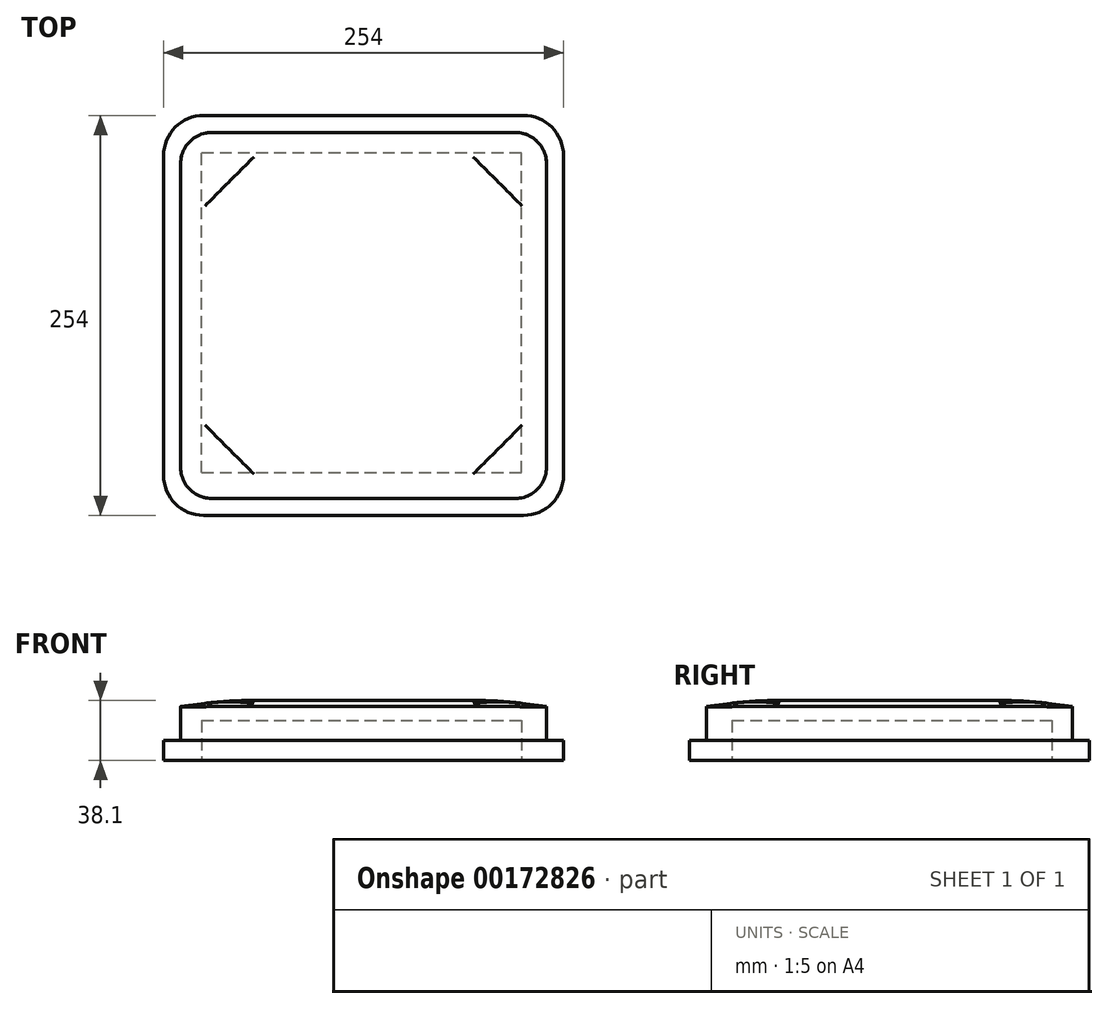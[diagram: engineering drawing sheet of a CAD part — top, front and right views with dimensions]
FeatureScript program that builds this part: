
annotation { "Feature Type Name" : "Feature", "Feature Type Description" : "" }
export const myFeature = defineFeature(function(context is Context, id is Id, definition is map)
    precondition{}
    {
        {
            var Q0;
            Q0=qCreatedBy(makeId("Top.planeOp"),FACE);
            var sketch = newSketch(context, id + "F0", { "sketchPlane" : qUnion([Q0])});
            skLineSegment(sketch, "E0.bottom", {"start": v(-176.99, 231.22) * mm, "end": v(26.21, 231.22) * mm});
            skLineSegment(sketch, "E0.top", {"start": v(-176.99, -22.78) * mm, "end": v(26.21, -22.78) * mm});
            skLineSegment(sketch, "E0.left", {"start": v(-202.39, 205.82) * mm, "end": v(-202.39, 2.62) * mm});
            skLineSegment(sketch, "E0.right", {"start": v(51.61, 205.82) * mm, "end": v(51.61, 2.62) * mm});
            skPoint(sketch, "E1.visualSharp", {"position": v(-202.39, 231.22) * mm});
            skArc(sketch, "E1.filletArc", {"start": v(-176.99, 231.22) * mm, "mid": v(-194.95, 223.78) * mm, "end": v(-202.39, 205.82) * mm});
            skPoint(sketch, "E2.visualSharp", {"position": v(51.61, 231.22) * mm});
            skArc(sketch, "E2.filletArc", {"start": v(51.61, 205.82) * mm, "mid": v(44.17, 223.78) * mm, "end": v(26.21, 231.22) * mm});
            skPoint(sketch, "E3.visualSharp", {"position": v(51.61, -22.78) * mm});
            skArc(sketch, "E3.filletArc", {"start": v(26.21, -22.78) * mm, "mid": v(44.17, -15.34) * mm, "end": v(51.61, 2.62) * mm});
            skPoint(sketch, "E4.visualSharp", {"position": v(-202.39, -22.78) * mm});
            skArc(sketch, "E4.filletArc", {"start": v(-202.39, 2.62) * mm, "mid": v(-194.95, -15.34) * mm, "end": v(-176.99, -22.78) * mm});
            skSolve(sketch);
        }
        {
            var Q0;
            Q0=qCreatedBy(makeId("Top.planeOp"),FACE);
            var sketch = newSketch(context, id + "F1", { "sketchPlane" : qUnion([Q0])});
            skLineSegment(sketch, "E5.bottom", {"start": v(-171.78, 220.42) * mm, "end": v(21, 220.42) * mm});
            skLineSegment(sketch, "E5.top", {"start": v(-171.78, -11.99) * mm, "end": v(21, -11.99) * mm});
            skLineSegment(sketch, "E5.left", {"start": v(-191.6, 200.61) * mm, "end": v(-191.6, 7.83) * mm});
            skLineSegment(sketch, "E5.right", {"start": v(40.82, 200.61) * mm, "end": v(40.82, 7.83) * mm});
            skPoint(sketch, "E6.visualSharp", {"position": v(-191.6, 220.42) * mm});
            skArc(sketch, "E6.filletArc", {"start": v(-171.78, 220.42) * mm, "mid": v(-185.8, 214.62) * mm, "end": v(-191.6, 200.61) * mm});
            skPoint(sketch, "E7.visualSharp", {"position": v(40.82, 220.42) * mm});
            skArc(sketch, "E7.filletArc", {"start": v(40.82, 200.61) * mm, "mid": v(35.01, 214.62) * mm, "end": v(21, 220.42) * mm});
            skPoint(sketch, "E8.visualSharp", {"position": v(40.82, -11.99) * mm});
            skArc(sketch, "E8.filletArc", {"start": v(21, -11.99) * mm, "mid": v(35.01, -6.18) * mm, "end": v(40.82, 7.83) * mm});
            skPoint(sketch, "E9.visualSharp", {"position": v(-191.6, -11.99) * mm});
            skArc(sketch, "E9.filletArc", {"start": v(-191.6, 7.83) * mm, "mid": v(-185.8, -6.18) * mm, "end": v(-171.78, -11.99) * mm});
            skSolve(sketch);
        }
        {
            var Q0;
            Q0 = qSketchRegion(id + "F0", true);
            extrude(context, id + "F2", {"entities" : qUnion([Q0]), "depth" : 25.4 * mm});
        }
        {
            var Q0;
            Q0 = qSketchRegion(id + "F1", true);
            extrude(context, id + "F3", {"entities" : qUnion([Q0]), "operationType" : NewBodyOperationType.ADD, "depth" : 47 * mm});
        }
        {
            var Q0;
            Q0=makeQuery(id+"F3.opExtrude","CAP_FACE",FACE,{"disambiguationData":[OSD([sQuery(id+"F1.wireOp",EDGE,"E5.bottom"),sQuery(id+"F1.wireOp",EDGE,"E5.top"),sQuery(id+"F1.wireOp",EDGE,"E5.left"),sQuery(id+"F1.wireOp",EDGE,"E5.right"),sQuery(id+"F1.wireOp",EDGE,"E6.filletArc"),sQuery(id+"F1.wireOp",EDGE,"E7.filletArc"),sQuery(id+"F1.wireOp",EDGE,"E8.filletArc"),sQuery(id+"F1.wireOp",EDGE,"E9.filletArc")])],"isStart":false});
            extrude(context, id + "F4", {"entities" : qUnion([Q0]), "operationType" : NewBodyOperationType.ADD, "depth" : 3.8 * mm, "hasDraft" : true, "draftAngle" : 83 * degree, "draftPullDirection" : true});
        }
        {
            var Q0;
            {var subQ0=sQuery(id+"F1.wireOp",EDGE,"E8.filletArc");Q0=makeQuery(id+"F4.draft0.opDraft","MERGE",EDGE,{"derivedFrom":[makeQuery(id+"F4.opExtrude","SWEPT_EDGE",EDGE,{"disambiguationData":[OSD([sQuery(id+"F1.wireOp",EDGE,"E5.top"),subQ0])]}),makeQuery(id+"F4.opExtrude","SWEPT_EDGE",EDGE,{"disambiguationData":[OSD([sQuery(id+"F1.wireOp",EDGE,"E5.right"),subQ0])]})]});}
            var Q1;
            {var subQ0=sQuery(id+"F1.wireOp",EDGE,"E7.filletArc");Q1=makeQuery(id+"F4.draft0.opDraft","MERGE",EDGE,{"derivedFrom":[makeQuery(id+"F4.opExtrude","SWEPT_EDGE",EDGE,{"disambiguationData":[OSD([sQuery(id+"F1.wireOp",EDGE,"E5.bottom"),subQ0])]}),makeQuery(id+"F4.opExtrude","SWEPT_EDGE",EDGE,{"disambiguationData":[OSD([sQuery(id+"F1.wireOp",EDGE,"E5.right"),subQ0])]})]});}
            var Q2;
            {var subQ0=sQuery(id+"F1.wireOp",EDGE,"E6.filletArc");Q2=makeQuery(id+"F4.draft0.opDraft","MERGE",EDGE,{"derivedFrom":[makeQuery(id+"F4.opExtrude","SWEPT_EDGE",EDGE,{"disambiguationData":[OSD([sQuery(id+"F1.wireOp",EDGE,"E5.bottom"),subQ0])]}),makeQuery(id+"F4.opExtrude","SWEPT_EDGE",EDGE,{"disambiguationData":[OSD([sQuery(id+"F1.wireOp",EDGE,"E5.left"),subQ0])]})]});}
            var Q3;
            {var subQ0=sQuery(id+"F1.wireOp",EDGE,"E9.filletArc");Q3=makeQuery(id+"F4.draft0.opDraft","MERGE",EDGE,{"derivedFrom":[makeQuery(id+"F4.opExtrude","SWEPT_EDGE",EDGE,{"disambiguationData":[OSD([sQuery(id+"F1.wireOp",EDGE,"E5.top"),subQ0])]}),makeQuery(id+"F4.opExtrude","SWEPT_EDGE",EDGE,{"disambiguationData":[OSD([sQuery(id+"F1.wireOp",EDGE,"E5.left"),subQ0])]})]});}
            var Q4;
            Q4=makeQuery(id+"F4.opExtrude","CAP_EDGE",EDGE,{"disambiguationData":[OSD([sQuery(id+"F1.wireOp",EDGE,"E5.right")])],"isStart":false});
            var Q5;
            Q5=makeQuery(id+"F4.opExtrude","CAP_EDGE",EDGE,{"disambiguationData":[OSD([sQuery(id+"F1.wireOp",EDGE,"E5.top")])],"isStart":false});
            var Q6;
            Q6=makeQuery(id+"F4.opExtrude","CAP_EDGE",EDGE,{"disambiguationData":[OSD([sQuery(id+"F1.wireOp",EDGE,"E5.left")])],"isStart":false});
            var Q7;
            Q7=makeQuery(id+"F4.opExtrude","CAP_EDGE",EDGE,{"disambiguationData":[OSD([sQuery(id+"F1.wireOp",EDGE,"E5.bottom")])],"isStart":false});
            fillet(context, id + "F5", {"entities" : qUnion([Q0, Q1, Q2, Q3, Q4, Q5, Q6, Q7]), "radius" : 254 * mm, "tangentPropagation" : true, "allowEdgeOverflow" : false});
        }
        {
            var Q0;
            Q0=makeQuery(id+"F2.opExtrude","CAP_FACE",FACE,{"disambiguationData":[OSD([sQuery(id+"F0.wireOp",EDGE,"E0.bottom"),sQuery(id+"F0.wireOp",EDGE,"E0.top"),sQuery(id+"F0.wireOp",EDGE,"E0.left"),sQuery(id+"F0.wireOp",EDGE,"E0.right"),sQuery(id+"F0.wireOp",EDGE,"E1.filletArc"),sQuery(id+"F0.wireOp",EDGE,"E2.filletArc"),sQuery(id+"F0.wireOp",EDGE,"E3.filletArc"),sQuery(id+"F0.wireOp",EDGE,"E4.filletArc")])],"isStart":true});
            extrude(context, id + "F6", {"entities" : qUnion([Q0]), "operationType" : NewBodyOperationType.REMOVE, "oppositeDirection" : true, "depth" : 12.7 * mm});
        }
        {
            var Q0;
            Q0=makeQuery(id+"F6.boolean.opBoolean","COPY",FACE,{"derivedFrom":makeQuery(id+"F6.opExtrude","CAP_FACE",FACE,{"disambiguationData":[OSD([sQuery(id+"F0.wireOp",EDGE,"E0.bottom"),sQuery(id+"F0.wireOp",EDGE,"E0.top"),sQuery(id+"F0.wireOp",EDGE,"E0.left"),sQuery(id+"F0.wireOp",EDGE,"E0.right"),sQuery(id+"F0.wireOp",EDGE,"E1.filletArc"),sQuery(id+"F0.wireOp",EDGE,"E2.filletArc"),sQuery(id+"F0.wireOp",EDGE,"E3.filletArc"),sQuery(id+"F0.wireOp",EDGE,"E4.filletArc")])],"isStart":false})});
            var sketch = newSketch(context, id + "F7", { "sketchPlane" : qUnion([Q0])});
            skLineSegment(sketch, "E10.bottom", {"start": v(-178.14, -4.33) * mm, "end": v(25.06, -4.33) * mm});
            skLineSegment(sketch, "E10.top", {"start": v(-178.14, -207.53) * mm, "end": v(25.06, -207.53) * mm});
            skLineSegment(sketch, "E10.left", {"start": v(-178.14, -4.33) * mm, "end": v(-178.14, -207.53) * mm});
            skLineSegment(sketch, "E10.right", {"start": v(25.06, -4.33) * mm, "end": v(25.06, -207.53) * mm});
            skSolve(sketch);
        }
        {
            var Q0;
            Q0 = qSketchRegion(id + "F7", true);
            extrude(context, id + "F8", {"entities" : qUnion([Q0]), "operationType" : NewBodyOperationType.REMOVE, "oppositeDirection" : true, "depth" : 25.4 * mm});
        }
    });
